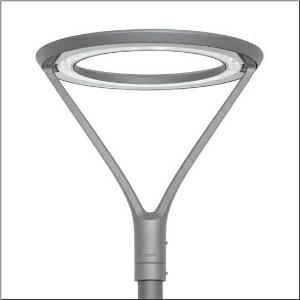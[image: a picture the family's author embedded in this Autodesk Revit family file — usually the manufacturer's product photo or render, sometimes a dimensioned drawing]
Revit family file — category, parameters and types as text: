
# Revit family: dl_r__20___pl1_2s_5xa51283ws008p_a586
name_source: partatom
category: Lighting Fixtures
units: mm (PartAtom-declared; Revit-internal decimal feet)

## family parameters
Cut with Voids When Loaded = No
Host = Face
Light Source = No
Part Type = Normal
Room Calculation Point = No
Round Connector Dimension = Use Diameter
Shared = No

## types (1)
- --- (1 x LED, 4250 lm, 34.3 W, 3000K)
    Apparent Load = 34 VA
    CIE Flux Codes = 33 78 99 100 100
    Color Rendering = 70
    Color Temperature = 3000K
    Default Elevation = 1800 mm
    Description = DL® 20, mast luminaire, primary light control with reflector, highly specular, primary optical cover: cover, of toughened safety glass of clear glass with excellent transmission level, light distribution: PL1.2s, light emission: direct distribution, primary light characteristic: symmetric, installation type: post-top, LED, High Power LED, rated luminous flux: 4.210lm, luminous efficacy: 80lm/W, light colour: 730, colour temperature: 3000K, control gear: Plus, control: overheat protection, power reduction, digital communication interface, constant luminous flux control, time-dependent luminous flux control, flexible luminous flux parameterisation, electronic power reduction, mains connection: 230..240V, 50/60Hz, connection cable pre-assembled, cable length: 5m, start of lifetime: 53W, end of service life: 54W, reduction: 24W, luminaire housing, upper part, of cast aluminium, powder-coated, Siteco® metallic grey (DB 702S), diameter: 690mm, height: 690mm, spigot size: 76mm (post-top), mounting height: 4..6m, luminaire housing, of cast aluminium, powder-coated, Siteco® metallic grey (DB 702S), equipment: Power, protection rating (complete): IP66, insulation class (complete): insulation class II (safety insulation), certification: CE, ENEC, VDE, impact resistance: IK08, permissible operating ambient temperature: -25..+30°C, standard-compliant lighting for roads and squares, packaging unit: 1 piece

Light Distribution: PL1.2s
    Height = 690 mm
    Lamp = 1 x LED
    Lamp Light Flux = 4250 lm
    Lamp Power = 34.3 W
    Lamp count = 1
    Length = 690 mm
    Luminous efficacy = 124 lm/W
    Manufacturer = Siteco
    ModVariant = No
    Model = 5XA51283WS008P
    Number of Poles = 1
    OnlyDefault = Yes
    Power Factor = 1
    Product Name = DL® 20 | PL1.2s
    Product group = mast luminaire | pylon top
    ProductGroupID = 6100
    Protection Class = Protection class II
    Protection Degree = IP 66
    RLX_Detail_Level = 1
    RLX_Emergency_Light_Flux = 0 lm
    RLX_Emergency_Type = 0
    RLX_Emergency_Type_DB = No
    RlxData = <blob elided: 204525 chars, md5=8eaf7c70>
    Socket = socket
    Standby Power = 0 W
    System Light Flux = 4250 lm
    System Power = 34 W
    Type Comments = factory setting: luminous flux: 100 % | dim-lin: 254 | 464 mA
    Type Image = l_1006001.jpg
    URL = http://relux.com
    VarID = @adj_076902
    Voltage = 0 V
    Weight = 0.00 kg
    Width = 0 mm  [stored 0 ft]

note: [stored X ft] marks values corroborated as IEEE doubles in the binary element streams (Revit-internal decimal feet)

## geometry (parser evidence)
native form markers: Blend x4, Sweep x11
no freeform markers — native parametric forms only
